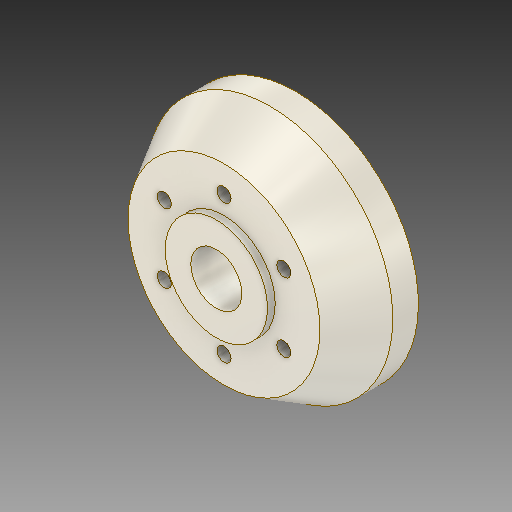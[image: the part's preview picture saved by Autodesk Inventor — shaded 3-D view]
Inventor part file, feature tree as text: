
AUTODESK INVENTOR PART (.ipt)
format: ipt  version: 2019 (Build 230136000, 136)  size: 183,808 bytes
history: native  units: mm
features: sketch x4, extrude x2, revolve x1, hole x1, thread x1, pattern_circular x1
ambient origin geometry x8: Origin, YZ Plane, XZ Plane, XY Plane, X Axis, Y Axis, Z Axis, Center Point
bodies: Solid1 (feature_tree)
feature tree (10):
  revolve  "Revolution1"  [1 undecoded]
  extrude  "Extrusion1"  Depth=10.0mm
  extrude  "Extrusion2"  Depth=10.0mm
  hole  "Hole1"  [1 undecoded]
  thread  "Thread2"  [1 undecoded]
  pattern_circular  "Circular Pattern1"  [2 undecoded]
  sketch  "Sketch1"  dims[d0=18.0mm d6=75.0mm]
  sketch  "Sketch2"  dims[d7=96.0mm d9=10.0mm]
  sketch  "Sketch3"  dims[d10=10.0mm d11=2.0mm]
  sketch  "Sketch4"  dims[d12=2.0mm d13=90.0deg d14=40.0mm d15=3.0mm d16=0.0mm d17=20.0mm d18=3.0mm d19=0.0mm d20=27.0mm d21=5.5mm d22=12.7mm d23=4.0mm d24=2.0mm d25=90.0deg d26=8.0mm d27=20.594885mm d30=60.0mm d31=360.0deg d33=0.624793mm d34=10.821mm d35=10.0mm d36=0.0mm]
note: 5 required parameter values undecoded (feature->parameter linkage not recoverable at this tier; creation-order binding heuristic only, values carry confidence <= 0.55)